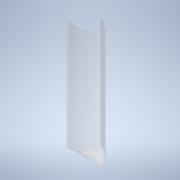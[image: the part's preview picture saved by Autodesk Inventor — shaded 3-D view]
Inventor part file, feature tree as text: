
AUTODESK INVENTOR PART (.ipt)
format: ipt  version: 2022 (Build 260153070, 153G)  size: 4,748,800 bytes
history: native  units: mm
features: sketch x8, extrude x8, other x5, plane x5, thicken_offset x3, fillet x1, projected_geometry x1, surface_op x1
ambient origin geometry x8: Origin, YZ Plane, XZ Plane, XY Plane, X Axis, Y Axis, Z Axis, Center Point
bodies: Body1 (feature_tree), Body2 (feature_tree), Body3 (feature_tree), Body4 (feature_tree)
feature tree (32):
  other  "Work Axis1"
  plane  "Work Plane1"
  sketch  "Sketch3"  dims[d10=1.5875mm d11=0.1mm d13=19.05mm]
  plane  "Work Plane3"
  thicken_offset  "Thicken2"
  thicken_offset  "Thicken6"
  other  "Work Axis3"
  plane  "Work Plane5"
  sketch  "Sketch6"  dims[d24=24.0mm d27=0.0mm d28=0.0mm]
  extrude  "Extrusion2"  Depth=10.0mm TaperAngle=0.0deg
  extrude  "Extrusion3"  TaperAngle=0.0deg  [1 undecoded]
  extrude  "Extrusion4"  Depth=19.05mm
  extrude  "Extrusion1"  Depth=395.5mm TaperAngle=0.0deg
  plane  "Work Plane9"
  fillet  "Fillet1"  Radius=5.0mm
  extrude  "Extrusion5"  Depth=40.0mm
  thicken_offset  "Thicken7"
  extrude  "Extrusion8"  TaperAngle=0.0deg  [1 undecoded]
  sketch  "Sketch1"  dims[d0=45.72mm d1=0.0mm d2=10.0mm d3=0.0mm]
  other  "Srf1"
  sketch  "Sketch2"  dims[d8=5.0mm d9=0.0mm]
  other  "Srf2"
  sketch  "Sketch4"  dims[d14=75.692mm d15=395.5mm d16=0.0mm d17=5.0mm]
  other  "Srf4"
  sketch  "Sketch5"  dims[d20=58.0mm d23=40.0mm]
  plane  "Work Plane8"
  sketch  "Sketch9"  dims[d29=3.0mm d30=3.0mm d31=200.0mm]
  projected_geometry  "Projected Loop1"
  sketch  "Sketch13"  dims[d32=144.5mm d33=0.0mm d34=250.0mm d35=0.0mm d36=3.0mm d37=2.0mm d38=2.0mm d39=0.0mm d40=3.0mm d41=5.0mm d51=20.0mm d52=10.0mm d53=2.0mm d54=0.0mm]
  extrude  "ExtrusionSrf1"  Depth=200.0mm
  extrude  "ExtrusionSrf2"  Depth=10.0mm TaperAngle=0.0deg
  surface_op  "Boundary Patch2"
note: 2 required parameter values undecoded (feature->parameter linkage not recoverable at this tier; creation-order binding heuristic only, values carry confidence <= 0.55)
